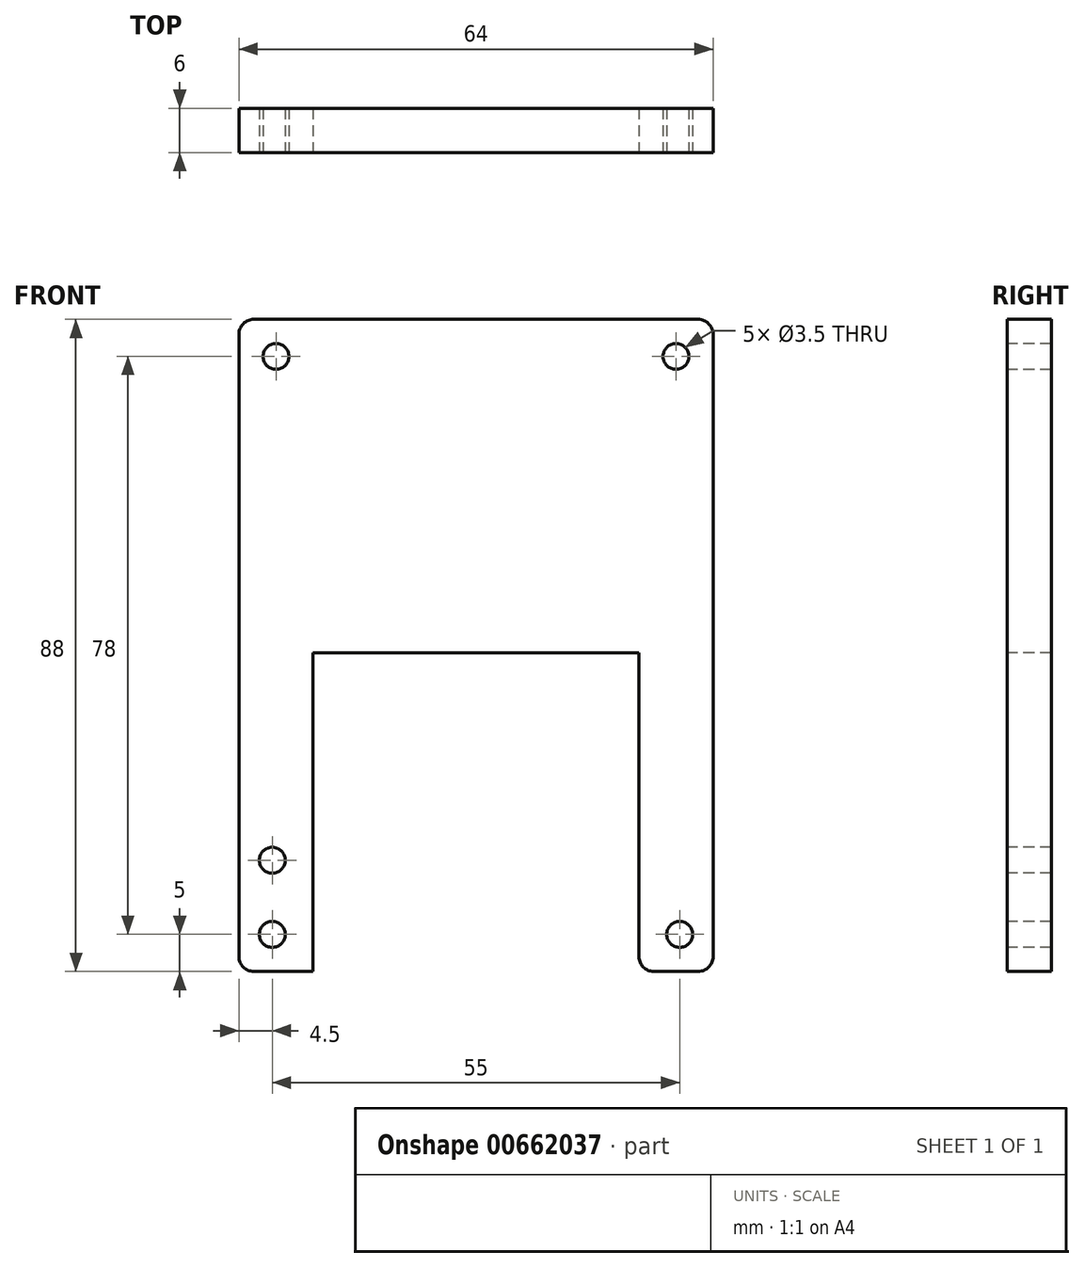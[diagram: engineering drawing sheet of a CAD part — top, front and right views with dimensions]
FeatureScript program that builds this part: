
annotation { "Feature Type Name" : "Feature", "Feature Type Description" : "" }
export const myFeature = defineFeature(function(context is Context, id is Id, definition is map)
    precondition{}
    {
        {
            var Q0;
            Q0=qCreatedBy(makeId("Front.planeOp"),FACE);
            var sketch = newSketch(context, id + "F0", { "sketchPlane" : qUnion([Q0])});
            skLineSegment(sketch, "E0.bottom", {"start": v(-32, 44) * mm, "end": v(32, 44) * mm});
            skLineSegment(sketch, "E0.top", {"start": v(-32, -44) * mm, "end": v(32, -44) * mm});
            skLineSegment(sketch, "E0.left", {"start": v(-32, 44) * mm, "end": v(-32, -44) * mm});
            skLineSegment(sketch, "E0.right", {"start": v(32, 44) * mm, "end": v(32, -44) * mm});
            skPoint(sketch, "E0.middle", {"position": v(0, 0) * mm});
            skSolve(sketch);
        }
        {
            var Q0;
            Q0=qSketchRegion(id+"F0",true);
            extrude(context, id + "F1", {"entities" : qUnion([Q0]), "depth" : 6 * mm, "offsetDistance" : 25 * mm});
        }
        {
            var Q0;
            Q0=makeQuery(id+"F1.opExtrude","CAP_FACE",FACE,{"disambiguationData":[OSD([sQuery(id+"F0.wireOp",EDGE,"E0.bottom"),sQuery(id+"F0.wireOp",EDGE,"E0.top"),sQuery(id+"F0.wireOp",EDGE,"E0.left"),sQuery(id+"F0.wireOp",EDGE,"E0.right")])],"isStart":false});
            var sketch = newSketch(context, id + "F2", { "sketchPlane" : qUnion([Q0])});
            skLineSegment(sketch, "E1.bottom", {"start": v(-32, 44) * mm, "end": v(32, 44) * mm});
            skLineSegment(sketch, "E1.top", {"start": v(-32, 34) * mm, "end": v(32, 34) * mm});
            skLineSegment(sketch, "E1.left", {"start": v(-32, 44) * mm, "end": v(-32, 34) * mm});
            skLineSegment(sketch, "E1.right", {"start": v(32, 44) * mm, "end": v(32, 34) * mm});
            skLineSegment(sketch, "E2", {"start": v(-32, 44) * mm, "end": v(-27, 44) * mm});
            skLineSegment(sketch, "E3", {"start": v(32, 44) * mm, "end": v(27, 44) * mm});
            skPoint(sketch, "E4.centerSnap0", {"position": v(-32, 39) * mm});
            skLineSegment(sketch, "E5.bottom", {"start": v(-32, -44) * mm, "end": v(-23, -44) * mm});
            skLineSegment(sketch, "E5.top", {"start": v(-32, -24) * mm, "end": v(-23, -24) * mm});
            skLineSegment(sketch, "E5.left", {"start": v(-32, -44) * mm, "end": v(-32, -24) * mm});
            skLineSegment(sketch, "E5.right", {"start": v(-23, -44) * mm, "end": v(-23, -24) * mm});
            skLineSegment(sketch, "E6.bottom", {"start": v(32, -44) * mm, "end": v(23, -44) * mm});
            skLineSegment(sketch, "E6.top", {"start": v(32, -24) * mm, "end": v(23, -24) * mm});
            skLineSegment(sketch, "E6.left", {"start": v(32, -44) * mm, "end": v(32, -24) * mm});
            skLineSegment(sketch, "E6.right", {"start": v(23, -44) * mm, "end": v(23, -34) * mm});
            skLineSegment(sketch, "E7", {"start": v(23, -34) * mm, "end": v(23, -24) * mm});
            skPoint(sketch, "E8.centerSnap0", {"position": v(27.5, -24) * mm});
            skPoint(sketch, "E8.centerSnap1", {"position": v(23, -29) * mm});
            skCircle(sketch, "E9", {"center": v(27.5, -39) * mm, "radius": 1.75 * mm});
            skPoint(sketch, "E9.centerSnap0", {"position": v(27.5, -44) * mm});
            skPoint(sketch, "E9.centerSnap1", {"position": v(23, -39) * mm});
            skCircle(sketch, "E10", {"center": v(-27.5, -29) * mm, "radius": 1.75 * mm});
            skPoint(sketch, "E10.centerSnap0", {"position": v(-27.5, -24) * mm});
            skCircle(sketch, "E11", {"center": v(-27.5, -39) * mm, "radius": 1.75 * mm});
            skPoint(sketch, "E11.centerSnap0", {"position": v(-27.5, -44) * mm});
            skLineSegment(sketch, "E12", {"start": v(0, 34) * mm, "end": v(0, -1) * mm});
            skLineSegment(sketch, "E13", {"start": v(0, -1) * mm, "end": v(-22, -1) * mm});
            skLineSegment(sketch, "E14.bottom", {"start": v(-22, -1) * mm, "end": v(22, -1) * mm});
            skLineSegment(sketch, "E14.top", {"start": v(-22, -45) * mm, "end": v(22, -45) * mm});
            skLineSegment(sketch, "E14.left", {"start": v(-22, -1) * mm, "end": v(-22, -45) * mm});
            skLineSegment(sketch, "E14.right", {"start": v(22, -1) * mm, "end": v(22, -45) * mm});
            skCircle(sketch, "E15", {"center": v(-27, 39) * mm, "radius": 1.75 * mm});
            skCircle(sketch, "E16", {"center": v(27, 39) * mm, "radius": 1.75 * mm});
            skSolve(sketch);
        }
        {
            var Q0;
            Q0=makeQuery(id+"F2.imprint","IMPRINT",FACE,{"disambiguationData":[TD([[makeQuery(id+"F2.imprint","IMPRINT",EDGE,{"derivedFrom":sQuery(id+"F2.wireOp",EDGE,"E4")}),1.0]])]});
            var Q1;
            Q1=makeQuery(id+"F2.imprint","IMPRINT",FACE,{"disambiguationData":[TD([[makeQuery(id+"F2.imprint","IMPRINT",EDGE,{"derivedFrom":sQuery(id+"F2.wireOp",EDGE,"QQvlmPxO-cxej-femh-iUQz-XWaODElKWglP")}),1.0]])]});
            var Q2;
            Q2=makeQuery(id+"F2.imprint","IMPRINT",FACE,{"disambiguationData":[TD([[makeQuery(id+"F2.imprint","IMPRINT",EDGE,{"derivedFrom":sQuery(id+"F2.wireOp",EDGE,"E8")}),1.0]])]});
            var Q3;
            Q3=makeQuery(id+"F2.imprint","IMPRINT",FACE,{"disambiguationData":[TD([[makeQuery(id+"F2.imprint","IMPRINT",EDGE,{"derivedFrom":sQuery(id+"F2.wireOp",EDGE,"E9")}),1.0]])]});
            var Q4;
            Q4=makeQuery(id+"F2.imprint","IMPRINT",FACE,{"disambiguationData":[TD([[makeQuery(id+"F2.imprint","IMPRINT",EDGE,{"derivedFrom":sQuery(id+"F2.wireOp",EDGE,"E10")}),1.0]])]});
            var Q5;
            Q5=makeQuery(id+"F2.imprint","IMPRINT",FACE,{"disambiguationData":[TD([[makeQuery(id+"F2.imprint","IMPRINT",EDGE,{"derivedFrom":sQuery(id+"F2.wireOp",EDGE,"E11")}),1.0]])]});
            var Q6;
            {var subQ1=sQuery(id+"F2.wireOp",EDGE,"E14.bottom");var subQ5=makeQuery(id+"F2.imprint","INTERSECT",VERTEX,{"derivedFrom":[sQuery(id+"F2.wireOp",EDGE,"E12"),subQ1]});Q6=makeQuery(id+"F2.imprint","IMPRINT",FACE,{"disambiguationData":[TD([[makeQuery(id+"F2.imprint","IMPRINT",EDGE,{"disambiguationData":[TD([[subQ5,1.0]])],"derivedFrom":subQ1}),-1.0]])]});}
            var Q7;
            Q7=makeQuery(id+"F2.imprint","IMPRINT",FACE,{"disambiguationData":[TD([[makeQuery(id+"F2.imprint","IMPRINT",EDGE,{"derivedFrom":sQuery(id+"F2.wireOp",EDGE,"E15")}),1.0]])]});
            var Q8;
            Q8=makeQuery(id+"F2.imprint","IMPRINT",FACE,{"disambiguationData":[TD([[makeQuery(id+"F2.imprint","IMPRINT",EDGE,{"derivedFrom":sQuery(id+"F2.wireOp",EDGE,"E16")}),1.0]])]});
            extrude(context, id + "F3", {"entities" : qUnion([Q0, Q1, Q2, Q3, Q4, Q5, Q6, Q7, Q8]), "operationType" : NewBodyOperationType.REMOVE, "oppositeDirection" : true, "depth" : 25 * mm, "offsetDistance" : 25 * mm});
        }
        {
            var Q0;
            Q0=makeQuery(id+"F1.opExtrude","SWEPT_EDGE",EDGE,{"disambiguationData":[OSD([sQuery(id+"F0.wireOp",EDGE,"E0.bottom"),sQuery(id+"F0.wireOp",EDGE,"E0.left")])]});
            var Q1;
            Q1=makeQuery(id+"F1.opExtrude","SWEPT_EDGE",EDGE,{"disambiguationData":[OSD([sQuery(id+"F0.wireOp",EDGE,"E0.bottom"),sQuery(id+"F0.wireOp",EDGE,"E0.right")])]});
            var Q2;
            Q2=makeQuery(id+"F1.opExtrude","SWEPT_EDGE",EDGE,{"disambiguationData":[OSD([sQuery(id+"F0.wireOp",EDGE,"E0.top"),sQuery(id+"F0.wireOp",EDGE,"E0.left")])]});
            var Q3;
            Q3=makeQuery(id+"F1.opExtrude","SWEPT_EDGE",EDGE,{"disambiguationData":[OSD([sQuery(id+"F0.wireOp",EDGE,"E0.top"),sQuery(id+"F0.wireOp",EDGE,"E0.right")])]});
            var Q4;
            Q4=makeQuery(id+"F3.boolean.opBoolean","COPY",EDGE,{"derivedFrom":makeQuery(id+"F3.opExtrude","SWEPT_EDGE",EDGE,{"disambiguationData":[OSD([sQuery(id+"F0.wireOp",EDGE,"E0.top"),sQuery(id+"F2.wireOp",EDGE,"E14.left")])]})});
            var Q5;
            Q5=makeQuery(id+"F3.boolean.opBoolean","COPY",EDGE,{"derivedFrom":makeQuery(id+"F3.opExtrude","SWEPT_EDGE",EDGE,{"disambiguationData":[OSD([sQuery(id+"F0.wireOp",EDGE,"E0.top"),sQuery(id+"F2.wireOp",EDGE,"E14.right")])]})});
            fillet(context, id + "F4", {"entities" : qUnion([Q0, Q1, Q2, Q3, Q4, Q5]), "radius" : 2 * mm, "tangentPropagation" : true, "allowEdgeOverflow" : false});
        }
    });
